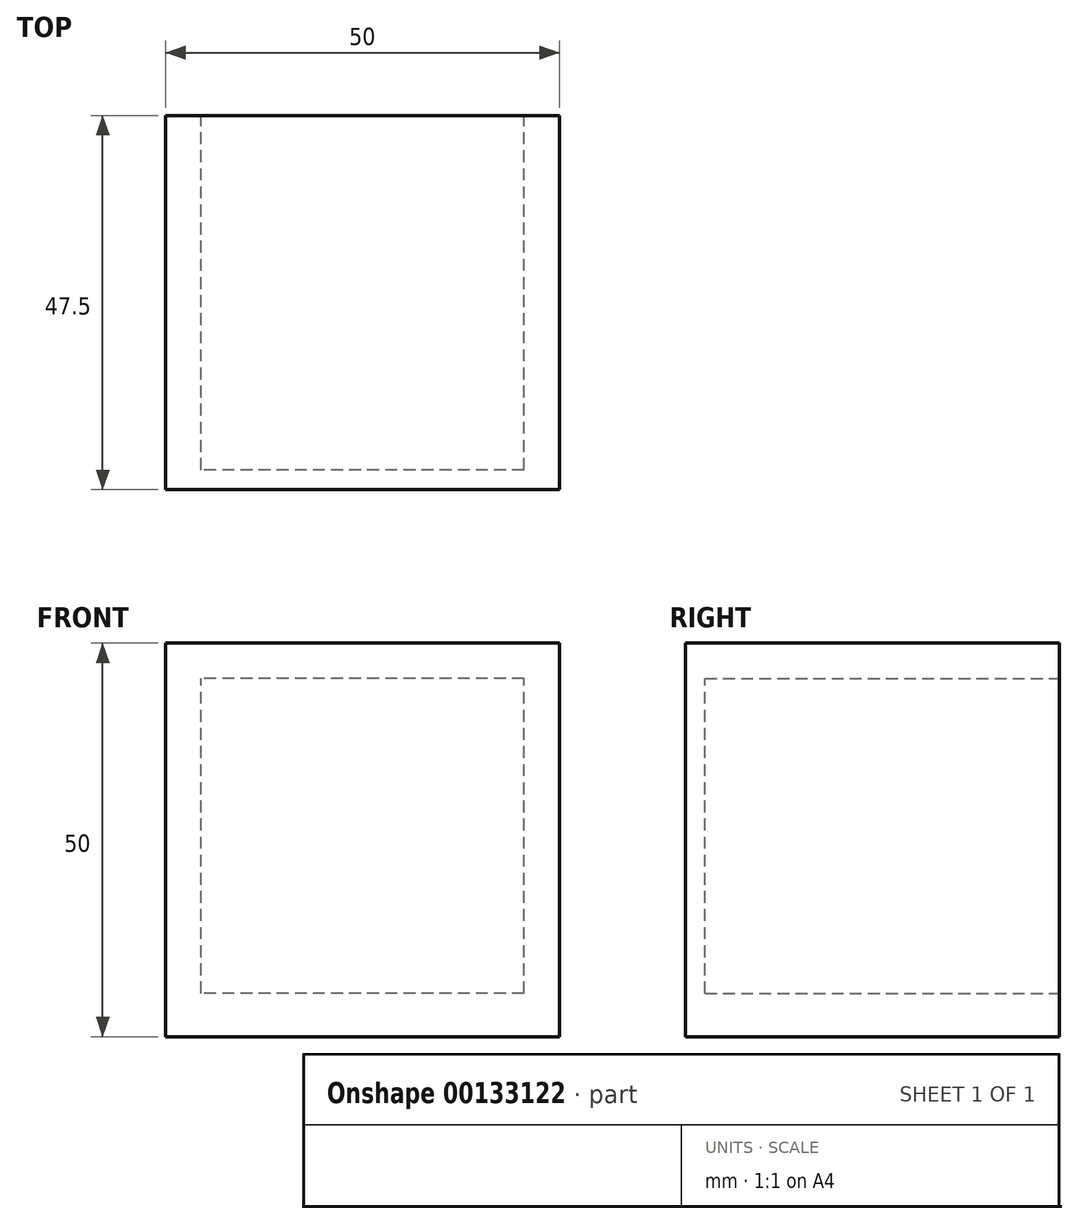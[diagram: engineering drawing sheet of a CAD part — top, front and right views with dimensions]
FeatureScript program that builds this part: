
annotation { "Feature Type Name" : "Feature", "Feature Type Description" : "" }
export const myFeature = defineFeature(function(context is Context, id is Id, definition is map)
    precondition{}
    {
        {
            var Q0;
            Q0=qCreatedBy(makeId("Front.planeOp"),FACE);
            var sketch = newSketch(context, id + "F0", { "sketchPlane" : qUnion([Q0])});
            skLineSegment(sketch, "E0.bottom", {"start": v(-39.97, 26.41) * mm, "end": v(10.03, 26.41) * mm});
            skLineSegment(sketch, "E0.top", {"start": v(-39.97, -23.59) * mm, "end": v(10.03, -23.59) * mm});
            skLineSegment(sketch, "E0.left", {"start": v(-39.97, 26.41) * mm, "end": v(-39.97, -23.59) * mm});
            skLineSegment(sketch, "E0.right", {"start": v(10.03, 26.41) * mm, "end": v(10.03, -23.59) * mm});
            skLineSegment(sketch, "E1.bottom", {"start": v(5.53, -18.09) * mm, "end": v(-35.47, -18.09) * mm});
            skLineSegment(sketch, "E1.top", {"start": v(5.53, 21.91) * mm, "end": v(-35.47, 21.91) * mm});
            skLineSegment(sketch, "E1.left", {"start": v(5.53, -18.09) * mm, "end": v(5.53, 21.91) * mm});
            skLineSegment(sketch, "E1.right", {"start": v(-35.47, -18.09) * mm, "end": v(-35.47, 21.91) * mm});
            skPoint(sketch, "E1.middle", {"position": v(-14.97, 1.91) * mm});
            skSolve(sketch);
        }
        {
            var Q0;
            {var subQ0=sQuery(id+"F0.wireOp",EDGE,"ViUHpMmo-JxAd-tFx5-wsu5-HmLKhpKHdZaX");var subQ1=sQuery(id+"F0.wireOp",EDGE,"sg4J9cJI-NK59-gakG-WzA0-6pr65WVGEJpl");var subQ2=makeQuery(id+"F0.imprint","INTERSECT",VERTEX,{"disambiguationData":[OD(0.0)],"derivedFrom":[subQ1,subQ0]});Q0=makeQuery(id+"F0.imprint","IMPRINT",FACE,{"disambiguationData":[TD([[makeQuery(id+"F0.imprint","IMPRINT",EDGE,{"disambiguationData":[TD([[subQ2,-1.0]])],"derivedFrom":subQ1}),-1.0]])]});}
            var Q1;
            {var subQ0=sQuery(id+"F0.wireOp",EDGE,"ViUHpMmo-JxAd-tFx5-wsu5-HmLKhpKHdZaX");var subQ1=sQuery(id+"F0.wireOp",EDGE,"sg4J9cJI-NK59-gakG-WzA0-6pr65WVGEJpl");var subQ2=makeQuery(id+"F0.imprint","INTERSECT",VERTEX,{"disambiguationData":[OD(0.0)],"derivedFrom":[subQ1,subQ0]});Q1=makeQuery(id+"F0.imprint","IMPRINT",FACE,{"disambiguationData":[TD([[makeQuery(id+"F0.imprint","IMPRINT",EDGE,{"disambiguationData":[TD([[subQ2,-1.0]])],"derivedFrom":subQ1}),1.0]])]});}
            var Q2;
            {var subQ0=sQuery(id+"F0.wireOp",EDGE,"RsLvm7Zy-Edqs-ZNfm-vyvg-IegkL9y1UujT");var subQ1=sQuery(id+"F0.wireOp",EDGE,"sg4J9cJI-NK59-gakG-WzA0-6pr65WVGEJpl");var subQ2=makeQuery(id+"F0.imprint","INTERSECT",VERTEX,{"derivedFrom":[subQ1,subQ0]});Q2=makeQuery(id+"F0.imprint","IMPRINT",FACE,{"disambiguationData":[TD([[makeQuery(id+"F0.imprint","IMPRINT",EDGE,{"disambiguationData":[TD([[subQ2,-1.0]])],"derivedFrom":subQ1}),1.0]])]});}
            var Q3;
            {var subQ0=sQuery(id+"F0.wireOp",EDGE,"RsLvm7Zy-Edqs-ZNfm-vyvg-IegkL9y1UujT");var subQ1=sQuery(id+"F0.wireOp",EDGE,"sg4J9cJI-NK59-gakG-WzA0-6pr65WVGEJpl");var subQ2=makeQuery(id+"F0.imprint","INTERSECT",VERTEX,{"derivedFrom":[subQ1,subQ0]});Q3=makeQuery(id+"F0.imprint","IMPRINT",FACE,{"disambiguationData":[TD([[makeQuery(id+"F0.imprint","IMPRINT",EDGE,{"disambiguationData":[TD([[subQ2,-1.0]])],"derivedFrom":subQ1}),-1.0]])]});}
            var Q4;
            {var subQ1=sQuery(id+"F0.wireOp",EDGE,"E1.top");var subQ5=sQuery(id+"F0.wireOp",EDGE,"E1.left");var subQ6=makeQuery(id+"F0.imprint","INTERSECT",VERTEX,{"derivedFrom":[subQ1,subQ5]});Q4=makeQuery(id+"F0.imprint","IMPRINT",FACE,{"disambiguationData":[TD([[makeQuery(id+"F0.imprint","IMPRINT",EDGE,{"disambiguationData":[TD([[subQ6,-1.0]])],"derivedFrom":subQ1}),1.0]])]});}
            var Q5;
            {var subQ1=sQuery(id+"F0.wireOp",EDGE,"E1.right");var subQ6=sQuery(id+"F0.wireOp",EDGE,"E1.top");var subQ9=makeQuery(id+"F0.imprint","INTERSECT",VERTEX,{"derivedFrom":[subQ6,subQ1]});Q5=makeQuery(id+"F0.imprint","IMPRINT",FACE,{"disambiguationData":[TD([[makeQuery(id+"F0.imprint","IMPRINT",EDGE,{"disambiguationData":[TD([[subQ9,1.0]])],"derivedFrom":subQ6}),1.0]])]});}
            var Q6;
            {var subQ1=sQuery(id+"F0.wireOp",EDGE,"E1.bottom");var subQ5=sQuery(id+"F0.wireOp",EDGE,"E1.left");var subQ6=makeQuery(id+"F0.imprint","INTERSECT",VERTEX,{"derivedFrom":[subQ1,subQ5]});Q6=makeQuery(id+"F0.imprint","IMPRINT",FACE,{"disambiguationData":[TD([[makeQuery(id+"F0.imprint","IMPRINT",EDGE,{"disambiguationData":[TD([[subQ6,-1.0]])],"derivedFrom":subQ1}),-1.0]])]});}
            var Q7;
            {var subQ1=sQuery(id+"F0.wireOp",EDGE,"E1.right");var subQ5=sQuery(id+"F0.wireOp",EDGE,"E1.bottom");var subQ6=makeQuery(id+"F0.imprint","INTERSECT",VERTEX,{"derivedFrom":[subQ5,subQ1]});Q7=makeQuery(id+"F0.imprint","IMPRINT",FACE,{"disambiguationData":[TD([[makeQuery(id+"F0.imprint","IMPRINT",EDGE,{"disambiguationData":[TD([[subQ6,1.0]])],"derivedFrom":subQ5}),-1.0]])]});}
            var Q8;
            Q8=makeQuery(id+"F0.imprint","IMPRINT",FACE,{"disambiguationData":[TD([[makeQuery(id+"F0.imprint","IMPRINT",EDGE,{"derivedFrom":sQuery(id+"F0.wireOp",EDGE,"E0.bottom")}),-1.0]])]});
            extrude(context, id + "F1", {"entities" : qUnion([Q0, Q1, Q2, Q3, Q4, Q5, Q6, Q7, Q8]), "depth" : 47.5 * mm});
        }
        {
            var Q0;
            Q0=makeQuery(id+"F0.imprint","IMPRINT",FACE,{"disambiguationData":[TD([[makeQuery(id+"F0.imprint","IMPRINT",EDGE,{"derivedFrom":sQuery(id+"F0.wireOp",EDGE,"E1.bottom")}),-1.0]])]});
            extrude(context, id + "F2", {"entities" : qUnion([Q0]), "operationType" : NewBodyOperationType.REMOVE, "depth" : 45 * mm});
        }
    });
